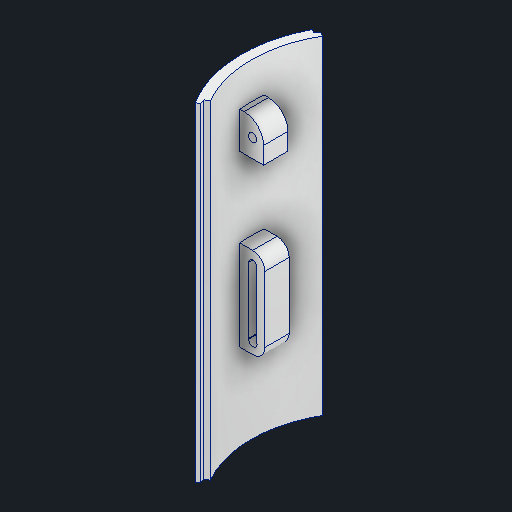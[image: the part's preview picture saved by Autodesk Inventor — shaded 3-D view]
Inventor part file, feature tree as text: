
AUTODESK INVENTOR PART (.ipt)
format: ipt  version: 2025.3 (Build 293356030, 356C)  size: 366,080 bytes
history: native  units: mm
features: sketch x8, extrude x5, other x3, projected_geometry x3, plane x2, fillet x2, hole x2
ambient origin geometry x8: Origin, YZ Plane, XZ Plane, XY Plane, X Axis, Y Axis, Z Axis, Center Point
bodies: Body1 (feature_tree)
feature tree (25):
  other  "Sólido1"
  extrude  "Extrusión1"  Depth=152.4mm TaperAngle=0.0deg
  other  "Labio1"
  other  "Labio2"
  plane  "Plano de trabajo2"
  extrude  "Extrusión2"  Depth=15.0mm
  fillet  "Empalme1"  Radius=10.0mm
  plane  "Plano de trabajo3"
  extrude  "Extrusión4"  Depth=8.0mm
  fillet  "Empalme2"  Radius=4.5mm
  sketch  "Boceto4"  dims[d30=8.0mm d32=3.0mm d33=4.5mm]
  extrude  "Extrusión5"  Depth=10.0mm
  extrude  "Extrusión6"  Depth=5.0mm
  hole  "Agujero1"  [1 undecoded]
  hole  "Agujero5"  [1 undecoded]
  sketch  "Boceto1"  dims[d1=30.0deg d3=152.4mm d4=0.0mm]
  sketch  "Boceto3"  dims[d5=2.0mm d6=2.0mm d7=0.0mm d8=0.0mm d9=15.0deg d10=0.0mm d11=2.0mm d12=2.0mm d13=0.0mm d14=0.0mm d15=15.0deg d16=0.0mm d26=15.0mm d28=10.0mm d29=0.0mm]
  projected_geometry  "Contorno proyectado2"
  projected_geometry  "Contorno proyectado3"
  sketch  "Boceto5"  dims[d37=10.0mm d38=53.0mm]
  sketch  "Boceto6"  dims[d39=10.5mm d40=0.0mm d41=5.0mm]
  sketch  "Boceto7"  dims[d43=3.15mm d44=10.0mm d45=0.0mm]
  projected_geometry  "Contorno proyectado4"
  sketch  "Boceto8"  dims[d46=130.0mm d47=90.0mm]
  sketch  "Boceto12"  dims[d48=17.701mm d49=0.0mm d51=3.4mm d52=6.0mm d53=6.3mm d54=2.0mm d55=90.0deg d56=8.0mm d57=20.594885mm d80=3.4mm d81=6.0mm d82=4.0mm d83=2.0mm d84=90.0deg d85=8.0mm d86=0.0mm d34=0.0mm d35=0.0mm d50=0.0mm]
note: 2 required parameter values undecoded (feature->parameter linkage not recoverable at this tier; creation-order binding heuristic only, values carry confidence <= 0.55)
